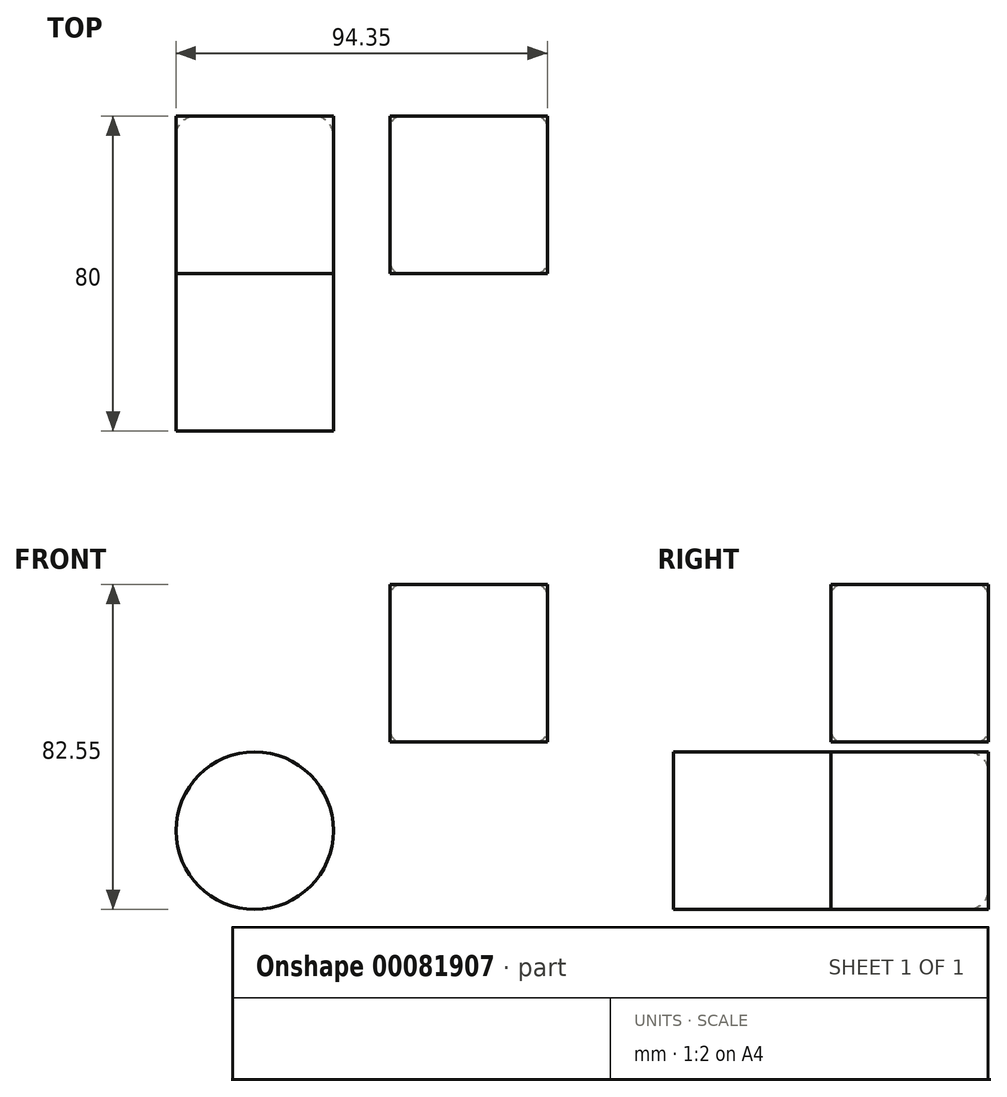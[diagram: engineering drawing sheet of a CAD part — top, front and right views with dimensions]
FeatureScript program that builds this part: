
annotation { "Feature Type Name" : "Feature", "Feature Type Description" : "" }
export const myFeature = defineFeature(function(context is Context, id is Id, definition is map)
    precondition{}
    {
        {
            var Q0;
            Q0=qCreatedBy(makeId("Front.planeOp"),FACE);
            var sketch = newSketch(context, id + "F0", { "sketchPlane" : qUnion([Q0])});
            skLineSegment(sketch, "E0.bottom", {"start": v(0, 0) * mm, "end": v(40, 0) * mm});
            skLineSegment(sketch, "E0.top", {"start": v(0, 40) * mm, "end": v(40, 40) * mm});
            skLineSegment(sketch, "E0.left", {"start": v(0, 0) * mm, "end": v(0, 40) * mm});
            skLineSegment(sketch, "E0.right", {"start": v(40, 0) * mm, "end": v(40, 40) * mm});
            skCircle(sketch, "E1", {"center": v(-34.35, -22.55) * mm, "radius": 20 * mm});
            skSolve(sketch);
        }
        {
            var Q0;
            Q0 = qSketchRegion(id + "F0", true);
            extrude(context, id + "F1", {"entities" : qUnion([Q0]), "depth" : 40 * mm});
        }
        {
            var Q0;
            Q0=makeQuery(id+"F1.opExtrude","SWEPT_FACE",FACE,{"disambiguationData":[OSD([sQuery(id+"F0.wireOp",EDGE,"E0.top")])]});
            var Q1;
            Q1=makeQuery(id+"F1.opExtrude","SWEPT_FACE",FACE,{"disambiguationData":[OSD([sQuery(id+"F0.wireOp",EDGE,"E0.right")])]});
            var Q2;
            Q2=makeQuery(id+"F1.opExtrude","CAP_FACE",FACE,{"disambiguationData":[OSD([sQuery(id+"F0.wireOp",EDGE,"E0.bottom"),sQuery(id+"F0.wireOp",EDGE,"E0.top"),sQuery(id+"F0.wireOp",EDGE,"E0.left"),sQuery(id+"F0.wireOp",EDGE,"E0.right")])],"isStart":false});
            var Q3;
            Q3=makeQuery(id+"F1.opExtrude","CAP_FACE",FACE,{"disambiguationData":[OSD([sQuery(id+"F0.wireOp",EDGE,"E0.bottom"),sQuery(id+"F0.wireOp",EDGE,"E0.top"),sQuery(id+"F0.wireOp",EDGE,"E0.left"),sQuery(id+"F0.wireOp",EDGE,"E0.right")])],"isStart":true});
            var Q4;
            Q4=makeQuery(id+"F1.opExtrude","SWEPT_FACE",FACE,{"disambiguationData":[OSD([sQuery(id+"F0.wireOp",EDGE,"E0.left")])]});
            fillet(context, id + "F2", {"entities" : qUnion([Q0, Q1, Q2, Q3, Q4]), "radius" : 3 * mm, "tangentPropagation" : true, "allowEdgeOverflow" : false});
        }
        {
            var Q0;
            Q0 = qSketchRegion(id + "F0", true);
            var Q1;
            Q1=makeQuery(id+"F1.opExtrude","CAP_FACE",FACE,{"disambiguationData":[OSD([sQuery(id+"F0.wireOp",EDGE,"E1")])],"isStart":false});
            extrude(context, id + "F3", {"entities" : qUnion([Q0, Q1]), "depth" : 40 * mm});
        }
        {
            var Q0;
            Q0=makeQuery(id+"F1.opExtrude","CAP_EDGE",EDGE,{"disambiguationData":[OSD([sQuery(id+"F0.wireOp",EDGE,"E1")])],"isStart":true});
            fillet(context, id + "F4", {"entities" : qUnion([Q0]), "radius" : 5 * mm, "tangentPropagation" : true, "allowEdgeOverflow" : false});
        }
    });
